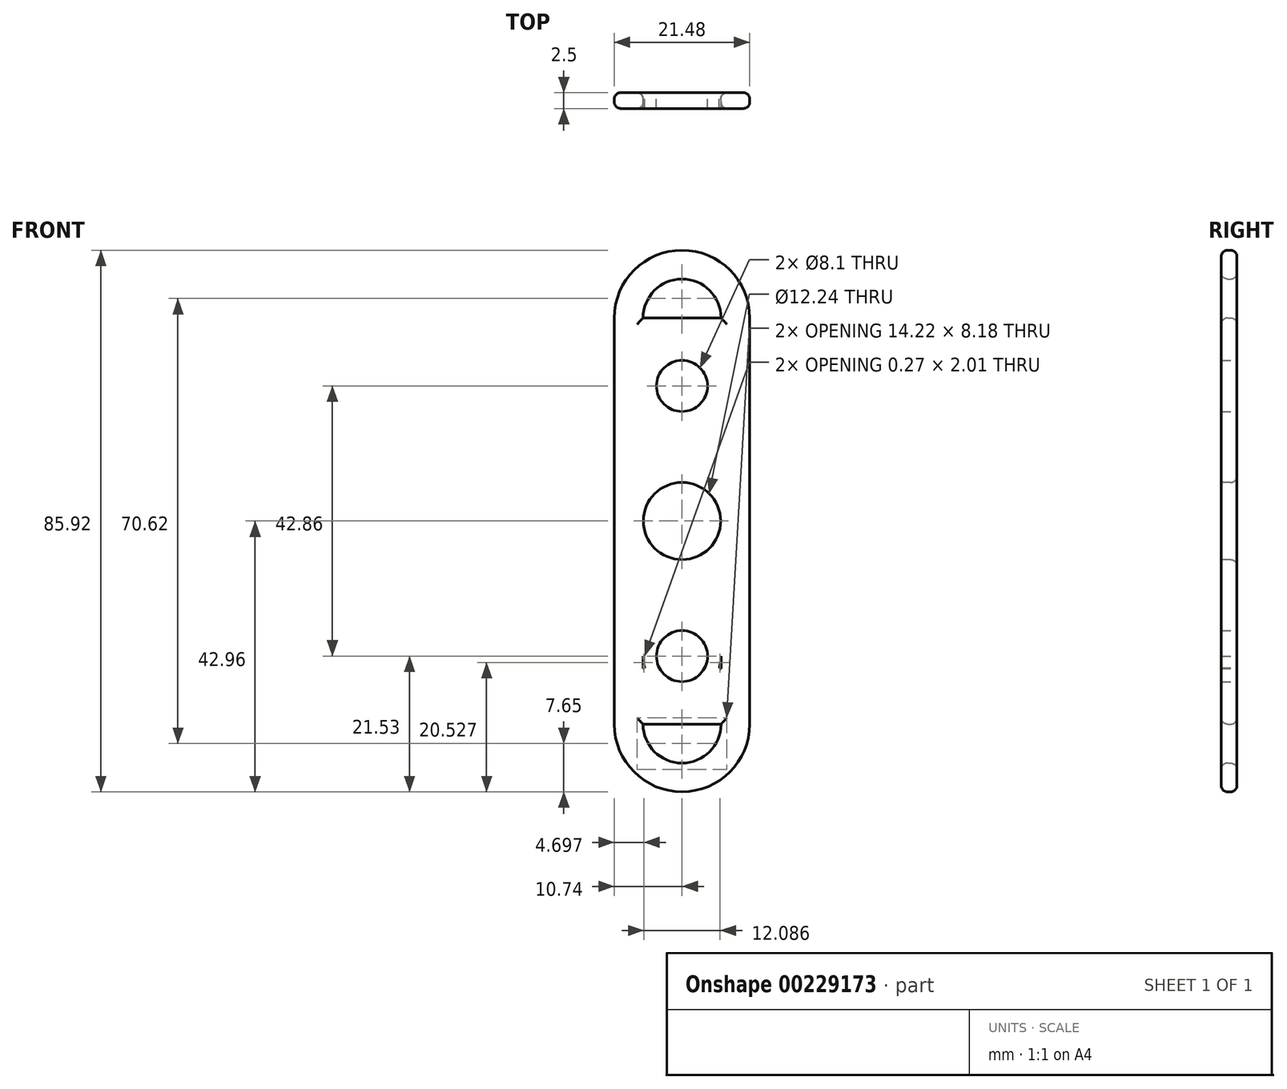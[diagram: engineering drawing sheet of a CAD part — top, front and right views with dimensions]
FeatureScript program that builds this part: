
annotation { "Feature Type Name" : "Feature", "Feature Type Description" : "" }
export const myFeature = defineFeature(function(context is Context, id is Id, definition is map)
    precondition{}
    {
        {
            var Q0;
            Q0=qCreatedBy(makeId("Front.planeOp"),FACE);
            var sketch = newSketch(context, id + "F0", { "sketchPlane" : qUnion([Q0])});
            skLineSegment(sketch, "E0.bottom", {"start": v(6.18, -11.5) * mm, "end": v(-6.18, -11.5) * mm});
            skLineSegment(sketch, "E0.top", {"start": v(6.18, 11.5) * mm, "end": v(-6.18, 11.5) * mm});
            skLineSegment(sketch, "E0.left", {"start": v(6.18, -11.5) * mm, "end": v(6.18, 11.5) * mm});
            skLineSegment(sketch, "E0.right", {"start": v(-6.18, -11.5) * mm, "end": v(-6.18, 11.5) * mm});
            skPoint(sketch, "E0.middle", {"position": v(0, 0) * mm});
            skLineSegment(sketch, "E1.bottom", {"start": v(6.18, -16.1) * mm, "end": v(-6.18, -16.1) * mm});
            skLineSegment(sketch, "E1.top", {"start": v(6.18, 16.1) * mm, "end": v(-6.18, 16.1) * mm});
            skLineSegment(sketch, "E1.left", {"start": v(6.18, -16.1) * mm, "end": v(6.18, 16.1) * mm});
            skLineSegment(sketch, "E1.right", {"start": v(-6.18, -16.1) * mm, "end": v(-6.18, 16.1) * mm});
            skLineSegment(sketch, "E2.left", {"start": v(10.74, -19) * mm, "end": v(10.74, 16.1) * mm});
            skLineSegment(sketch, "E2.right", {"start": v(-10.74, -19) * mm, "end": v(-10.74, 16.1) * mm});
            skLineSegment(sketch, "E3", {"start": v(-6.18, 16.1) * mm, "end": v(6.18, 11.5) * mm, "construction": true});
            skLineSegment(sketch, "E4", {"start": v(-6.18, 11.5) * mm, "end": v(6.18, 16.1) * mm, "construction": true});
            skArc(sketch, "E5", {"start": v(10.74, 16.1) * mm, "mid": v(0, 26.85) * mm, "end": v(-10.74, 16.1) * mm});
            skArc(sketch, "E6", {"start": v(6.18, 16.1) * mm, "mid": v(0, 22.29) * mm, "end": v(-6.18, 16.1) * mm});
            skCircle(sketch, "E7", {"center": v(0, 13.8) * mm, "radius": 1 * mm});
            skCircle(sketch, "E8", {"center": v(0, -13.8) * mm, "radius": 1 * mm});
            skLineSegment(sketch, "E9.bottom", {"start": v(-6.18, -48.33) * mm, "end": v(6.18, -48.33) * mm});
            skLineSegment(sketch, "E9.top", {"start": v(-6.18, -16.1) * mm, "end": v(6.18, -16.1) * mm});
            skLineSegment(sketch, "E9.left", {"start": v(-6.18, -48.33) * mm, "end": v(-6.18, -16.1) * mm});
            skLineSegment(sketch, "E9.right", {"start": v(6.18, -48.33) * mm, "end": v(6.18, -16.1) * mm});
            skLineSegment(sketch, "E10.bottom", {"start": v(6.18, -43.72) * mm, "end": v(-6.18, -43.72) * mm});
            skLineSegment(sketch, "E10.top", {"start": v(6.18, -20.72) * mm, "end": v(-6.18, -20.72) * mm});
            skLineSegment(sketch, "E10.left", {"start": v(6.18, -43.72) * mm, "end": v(6.18, -20.72) * mm});
            skLineSegment(sketch, "E10.right", {"start": v(-6.18, -43.72) * mm, "end": v(-6.18, -20.72) * mm});
            skLineSegment(sketch, "E11", {"start": v(-6.18, -43.72) * mm, "end": v(6.18, -48.33) * mm, "construction": true});
            skLineSegment(sketch, "E12", {"start": v(-6.18, -48.33) * mm, "end": v(6.18, -43.72) * mm, "construction": true});
            skCircle(sketch, "E13", {"center": v(0, -46.03) * mm, "radius": 1 * mm});
            skCircle(sketch, "E14", {"center": v(0, -23.42) * mm, "radius": 1 * mm});
            skPoint(sketch, "E15.center.orphan", {"position": v(0, -48.33) * mm});
            skPoint(sketch, "E16.centerSnap0", {"position": v(0, -16.1) * mm});
            skLineSegment(sketch, "E17", {"start": v(-6.18, -16.1) * mm, "end": v(-6.18, -16.1) * mm});
            skLineSegment(sketch, "E18", {"start": v(6.18, -16.1) * mm, "end": v(6.18, -16.1) * mm});
            skLineSegment(sketch, "E19", {"start": v(-10.74, -19) * mm, "end": v(-10.74, -48.33) * mm});
            skLineSegment(sketch, "E20", {"start": v(10.74, -19) * mm, "end": v(10.74, -48.33) * mm});
            skCircle(sketch, "E21", {"center": v(0, -48.33) * mm, "radius": 6.18 * mm});
            skCircle(sketch, "E22", {"center": v(0, -48.33) * mm, "radius": 10.74 * mm});
            skCircle(sketch, "E23", {"center": v(0, -37.54) * mm, "radius": 6.18 * mm});
            skCircle(sketch, "E24", {"center": v(0, 5.32) * mm, "radius": 6.18 * mm});
            skCircle(sketch, "E25", {"center": v(0, 5.32) * mm, "radius": 4.05 * mm});
            skCircle(sketch, "E26", {"center": v(0, -37.54) * mm, "radius": 4.05 * mm});
            skPoint(sketch, "E27.centerSnap0", {"position": v(6.18, -21.1) * mm});
            skSolve(sketch);
        }
        {
            var Q0;
            {var subQ4=sQuery(id+"F0.wireOp",EDGE,"E22");var subQ15=makeQuery(id+"F0.imprint","INTERSECT",VERTEX,{"derivedFrom":[sQuery(id+"F0.wireOp",EDGE,"E20"),subQ4]});Q0=makeQuery(id+"F0.imprint","IMPRINT",FACE,{"disambiguationData":[TD([[makeQuery(id+"F0.imprint","IMPRINT",EDGE,{"disambiguationData":[TD([[subQ15,-1.0]])],"derivedFrom":subQ4}),1.0]])]});}
            var Q1;
            Q1=makeQuery(id+"F0.imprint","IMPRINT",FACE,{"disambiguationData":[TD([[makeQuery(id+"F0.imprint","IMPRINT",EDGE,{"derivedFrom":sQuery(id+"F0.wireOp",EDGE,"E2.left")}),1.0]])]});
            var Q2;
            {var subQ1=sQuery(id+"F0.wireOp",EDGE,"E0.bottom");Q2=makeQuery(id+"F0.imprint","IMPRINT",FACE,{"disambiguationData":[TD([[makeQuery(id+"F0.imprint","IMPRINT",EDGE,{"derivedFrom":subQ1}),1.0]])]});}
            var Q3;
            {var subQ0=sQuery(id+"F0.wireOp",EDGE,"E0.bottom");Q3=makeQuery(id+"F0.imprint","IMPRINT",FACE,{"disambiguationData":[TD([[makeQuery(id+"F0.imprint","IMPRINT",EDGE,{"derivedFrom":subQ0}),-1.0]])]});}
            var Q4;
            {var subQ0=sQuery(id+"F0.wireOp",EDGE,"E22");var subQ1=sQuery(id+"F0.wireOp",EDGE,"E10.left");var subQ2=makeQuery(id+"F0.imprint","INTERSECT",VERTEX,{"derivedFrom":[subQ1,subQ0]});Q4=makeQuery(id+"F0.imprint","IMPRINT",FACE,{"disambiguationData":[TD([[makeQuery(id+"F0.imprint","IMPRINT",EDGE,{"disambiguationData":[TD([[subQ2,-1.0]])],"derivedFrom":subQ1}),1.0]])]});}
            var Q5;
            {var subQ0=sQuery(id+"F0.wireOp",EDGE,"E10.top");Q5=makeQuery(id+"F0.imprint","IMPRINT",FACE,{"disambiguationData":[TD([[makeQuery(id+"F0.imprint","IMPRINT",EDGE,{"derivedFrom":subQ0}),1.0]])]});}
            var Q6;
            {var subQ5=sQuery(id+"F0.wireOp",EDGE,"E21");var subQ6=sQuery(id+"F0.wireOp",EDGE,"E10.bottom");var subQ7=makeQuery(id+"F0.imprint","INTERSECT",VERTEX,{"disambiguationData":[OD(0.0)],"derivedFrom":[subQ6,subQ5]});Q6=makeQuery(id+"F0.imprint","IMPRINT",FACE,{"disambiguationData":[TD([[makeQuery(id+"F0.imprint","IMPRINT",EDGE,{"disambiguationData":[TD([[subQ7,-1.0]])],"derivedFrom":subQ5}),-1.0]])]});}
            var Q7;
            {var subQ0=sQuery(id+"F0.wireOp",EDGE,"E21");var subQ1=sQuery(id+"F0.wireOp",EDGE,"E10.bottom");var subQ2=makeQuery(id+"F0.imprint","INTERSECT",VERTEX,{"disambiguationData":[OD(0.0)],"derivedFrom":[subQ1,subQ0]});Q7=makeQuery(id+"F0.imprint","IMPRINT",FACE,{"disambiguationData":[TD([[makeQuery(id+"F0.imprint","IMPRINT",EDGE,{"disambiguationData":[TD([[subQ2,-1.0]])],"derivedFrom":subQ1}),-1.0]])]});}
            var Q8;
            {var subQ5=sQuery(id+"F0.wireOp",EDGE,"E9.bottom");Q8=makeQuery(id+"F0.imprint","IMPRINT",FACE,{"disambiguationData":[TD([[makeQuery(id+"F0.imprint","IMPRINT",EDGE,{"derivedFrom":subQ5}),1.0]])]});}
            var Q9;
            {var subQ0=sQuery(id+"F0.wireOp",EDGE,"E21");var subQ3=sQuery(id+"F0.wireOp",EDGE,"E10.bottom");var subQ5=makeQuery(id+"F0.imprint","INTERSECT",VERTEX,{"disambiguationData":[OD(1.0)],"derivedFrom":[subQ3,subQ0]});Q9=makeQuery(id+"F0.imprint","IMPRINT",FACE,{"disambiguationData":[TD([[makeQuery(id+"F0.imprint","IMPRINT",EDGE,{"disambiguationData":[TD([[subQ5,-1.0]])],"derivedFrom":subQ3}),1.0]])]});}
            var Q10;
            {var subQ0=sQuery(id+"F0.wireOp",EDGE,"E21");var subQ3=sQuery(id+"F0.wireOp",EDGE,"E10.bottom");var subQ5=makeQuery(id+"F0.imprint","INTERSECT",VERTEX,{"disambiguationData":[OD(0.0)],"derivedFrom":[subQ3,subQ0]});Q10=makeQuery(id+"F0.imprint","IMPRINT",FACE,{"disambiguationData":[TD([[makeQuery(id+"F0.imprint","IMPRINT",EDGE,{"disambiguationData":[TD([[subQ5,1.0]])],"derivedFrom":subQ3}),1.0]])]});}
            var Q11;
            {var subQ3=sQuery(id+"F0.wireOp",EDGE,"E10.top");Q11=makeQuery(id+"F0.imprint","IMPRINT",FACE,{"disambiguationData":[TD([[makeQuery(id+"F0.imprint","IMPRINT",EDGE,{"derivedFrom":subQ3}),-1.0]])]});}
            var Q12;
            Q12=makeQuery(id+"F0.imprint","IMPRINT",FACE,{"disambiguationData":[TD([[makeQuery(id+"F0.imprint","IMPRINT",EDGE,{"derivedFrom":sQuery(id+"F0.wireOp",EDGE,"E13")}),1.0]])]});
            var Q13;
            {var subQ5=sQuery(id+"F0.wireOp",EDGE,"E21");var subQ6=sQuery(id+"F0.wireOp",EDGE,"E10.bottom");var subQ7=makeQuery(id+"F0.imprint","INTERSECT",VERTEX,{"disambiguationData":[OD(1.0)],"derivedFrom":[subQ6,subQ5]});Q13=makeQuery(id+"F0.imprint","IMPRINT",FACE,{"disambiguationData":[TD([[makeQuery(id+"F0.imprint","IMPRINT",EDGE,{"disambiguationData":[TD([[subQ7,1.0]])],"derivedFrom":subQ5}),-1.0]])]});}
            var Q14;
            {var subQ0=sQuery(id+"F0.wireOp",EDGE,"E23");var subQ1=sQuery(id+"F0.wireOp",EDGE,"E10.bottom");var subQ2=makeQuery(id+"F0.imprint","INTERSECT",VERTEX,{"derivedFrom":[subQ1,subQ0]});Q14=makeQuery(id+"F0.imprint","IMPRINT",FACE,{"disambiguationData":[TD([[makeQuery(id+"F0.imprint","IMPRINT",EDGE,{"disambiguationData":[TD([[subQ2,-1.0]])],"derivedFrom":subQ1}),-1.0]])]});}
            var Q15;
            {var subQ0=sQuery(id+"F0.wireOp",EDGE,"E23");var subQ3=sQuery(id+"F0.wireOp",EDGE,"E22");var subQ8=makeQuery(id+"F0.imprint","INTERSECT",VERTEX,{"disambiguationData":[OD(0.0)],"derivedFrom":[subQ3,subQ0]});Q15=makeQuery(id+"F0.imprint","IMPRINT",FACE,{"disambiguationData":[TD([[makeQuery(id+"F0.imprint","IMPRINT",EDGE,{"disambiguationData":[TD([[subQ8,-1.0]])],"derivedFrom":subQ3}),-1.0]])]});}
            var Q16;
            {var subQ0=sQuery(id+"F0.wireOp",EDGE,"E23");var subQ1=sQuery(id+"F0.wireOp",EDGE,"E21");var subQ9=makeQuery(id+"F0.imprint","INTERSECT",VERTEX,{"disambiguationData":[OD(0.0)],"derivedFrom":[subQ1,subQ0]});Q16=makeQuery(id+"F0.imprint","IMPRINT",FACE,{"disambiguationData":[TD([[makeQuery(id+"F0.imprint","IMPRINT",EDGE,{"disambiguationData":[TD([[subQ9,-1.0]])],"derivedFrom":subQ1}),-1.0]])]});}
            var Q17;
            {var subQ0=sQuery(id+"F0.wireOp",EDGE,"E23");var subQ1=sQuery(id+"F0.wireOp",EDGE,"E21");var subQ2=makeQuery(id+"F0.imprint","INTERSECT",VERTEX,{"disambiguationData":[OD(0.0)],"derivedFrom":[subQ1,subQ0]});Q17=makeQuery(id+"F0.imprint","IMPRINT",FACE,{"disambiguationData":[TD([[makeQuery(id+"F0.imprint","IMPRINT",EDGE,{"disambiguationData":[TD([[subQ2,-1.0]])],"derivedFrom":subQ1}),1.0]])]});}
            var Q18;
            {var subQ0=sQuery(id+"F0.wireOp",EDGE,"E22");var subQ1=sQuery(id+"F0.wireOp",EDGE,"E10.right");var subQ2=makeQuery(id+"F0.imprint","INTERSECT",VERTEX,{"derivedFrom":[subQ1,subQ0]});Q18=makeQuery(id+"F0.imprint","IMPRINT",FACE,{"disambiguationData":[TD([[makeQuery(id+"F0.imprint","IMPRINT",EDGE,{"disambiguationData":[TD([[subQ2,-1.0]])],"derivedFrom":subQ1}),-1.0]])]});}
            var Q19;
            Q19=makeQuery(id+"F0.imprint","IMPRINT",FACE,{"disambiguationData":[TD([[makeQuery(id+"F0.imprint","IMPRINT",EDGE,{"derivedFrom":sQuery(id+"F0.wireOp",EDGE,"E25")}),-1.0]])]});
            var Q20;
            {var subQ0=sQuery(id+"F0.wireOp",EDGE,"E1.right");var subQ1=sQuery(id+"F0.wireOp",EDGE,"E0.top");var subQ2=makeQuery(id+"F0.imprint","INTERSECT",VERTEX,{"derivedFrom":[subQ1,subQ0]});Q20=makeQuery(id+"F0.imprint","IMPRINT",FACE,{"disambiguationData":[TD([[makeQuery(id+"F0.imprint","IMPRINT",EDGE,{"disambiguationData":[TD([[subQ2,1.0]])],"derivedFrom":subQ1}),1.0]])]});}
            var Q21;
            {var subQ4=sQuery(id+"F0.wireOp",EDGE,"E1.top");Q21=makeQuery(id+"F0.imprint","IMPRINT",FACE,{"disambiguationData":[TD([[makeQuery(id+"F0.imprint","IMPRINT",EDGE,{"derivedFrom":subQ4}),1.0]])]});}
            var Q22;
            {var subQ0=sQuery(id+"F0.wireOp",EDGE,"E1.left");var subQ1=sQuery(id+"F0.wireOp",EDGE,"E0.top");var subQ2=makeQuery(id+"F0.imprint","INTERSECT",VERTEX,{"derivedFrom":[subQ1,subQ0]});Q22=makeQuery(id+"F0.imprint","IMPRINT",FACE,{"disambiguationData":[TD([[makeQuery(id+"F0.imprint","IMPRINT",EDGE,{"disambiguationData":[TD([[subQ2,-1.0]])],"derivedFrom":subQ1}),1.0]])]});}
            var Q23;
            Q23=makeQuery(id+"F0.imprint","IMPRINT",FACE,{"disambiguationData":[TD([[makeQuery(id+"F0.imprint","IMPRINT",EDGE,{"derivedFrom":sQuery(id+"F0.wireOp",EDGE,"E7")}),1.0]])]});
            var Q24;
            Q24=makeQuery(id+"F0.imprint","IMPRINT",FACE,{"disambiguationData":[TD([[makeQuery(id+"F0.imprint","IMPRINT",EDGE,{"derivedFrom":sQuery(id+"F0.wireOp",EDGE,"E8")}),1.0]])]});
            var Q25;
            Q25=makeQuery(id+"F0.imprint","IMPRINT",FACE,{"disambiguationData":[TD([[makeQuery(id+"F0.imprint","IMPRINT",EDGE,{"derivedFrom":sQuery(id+"F0.wireOp",EDGE,"E14")}),-1.0]])]});
            var Q26;
            {var subQ0=sQuery(id+"F0.wireOp",EDGE,"E27");var subQ1=sQuery(id+"F0.wireOp",EDGE,"E1.bottom");var subQ2=makeQuery(id+"F0.imprint","INTERSECT",VERTEX,{"disambiguationData":[OD(0.0)],"derivedFrom":[subQ1,subQ0]});Q26=makeQuery(id+"F0.imprint","IMPRINT",FACE,{"disambiguationData":[TD([[makeQuery(id+"F0.imprint","IMPRINT",EDGE,{"disambiguationData":[TD([[subQ2,-1.0]])],"derivedFrom":subQ1}),-1.0]])]});}
            var Q27;
            {var subQ0=sQuery(id+"F0.wireOp",EDGE,"E27");var subQ1=sQuery(id+"F0.wireOp",EDGE,"E9.top");var subQ2=makeQuery(id+"F0.imprint","INTERSECT",VERTEX,{"disambiguationData":[OD(0.0)],"derivedFrom":[subQ1,subQ0]});Q27=makeQuery(id+"F0.imprint","IMPRINT",FACE,{"disambiguationData":[TD([[makeQuery(id+"F0.imprint","IMPRINT",EDGE,{"disambiguationData":[TD([[subQ2,-1.0]])],"derivedFrom":subQ1}),-1.0]])]});}
            var Q28;
            Q28=makeQuery(id+"F0.imprint","IMPRINT",FACE,{"disambiguationData":[TD([[makeQuery(id+"F0.imprint","IMPRINT",EDGE,{"derivedFrom":sQuery(id+"F0.wireOp",EDGE,"E14")}),1.0]])]});
            extrude(context, id + "F1", {"entities" : qUnion([Q0, Q1, Q2, Q3, Q4, Q5, Q6, Q7, Q8, Q9, Q10, Q11, Q12, Q13, Q14, Q15, Q16, Q17, Q18, Q19, Q20, Q21, Q22, Q23, Q24, Q25, Q26, Q27, Q28]), "depth" : 2.5 * mm});
        }
        {
            var Q0;
            Q0=makeQuery(id+"F1.opExtrude","CAP_FACE",FACE,{"disambiguationData":[OSD([sQuery(id+"F0.wireOp",EDGE,"E1.top"),sQuery(id+"F0.wireOp",EDGE,"E2.left"),sQuery(id+"F0.wireOp",EDGE,"E2.right"),sQuery(id+"F0.wireOp",EDGE,"E5"),sQuery(id+"F0.wireOp",EDGE,"E6"),sQuery(id+"F0.wireOp",EDGE,"E9.bottom"),sQuery(id+"F0.wireOp",EDGE,"E19"),sQuery(id+"F0.wireOp",EDGE,"E20"),sQuery(id+"F0.wireOp",EDGE,"E21"),sQuery(id+"F0.wireOp",EDGE,"E22"),sQuery(id+"F0.wireOp",EDGE,"E25"),sQuery(id+"F0.wireOp",EDGE,"E26")])],"isStart":false});
            var sketch = newSketch(context, id + "F2", { "sketchPlane" : qUnion([Q0])});
            skCircle(sketch, "E28", {"center": v(0, -16.1) * mm, "radius": 6.12 * mm});
            skSolve(sketch);
        }
        {
            var Q0;
            Q0=makeQuery(id+"F2.imprint","IMPRINT",FACE,{"disambiguationData":[TD([[makeQuery(id+"F2.imprint","IMPRINT",EDGE,{"derivedFrom":sQuery(id+"F2.wireOp",EDGE,"E28")}),1.0]])]});
            extrude(context, id + "F3", {"entities" : qUnion([Q0]), "operationType" : NewBodyOperationType.REMOVE, "oppositeDirection" : true, "depth" : 25 * mm});
        }
        {
            var Q0;
            Q0=makeQuery(id+"F1.opExtrude","CAP_EDGE",EDGE,{"disambiguationData":[OSD([sQuery(id+"F0.wireOp",EDGE,"E2.right"),sQuery(id+"F0.wireOp",EDGE,"E19")])],"isStart":false});
            var Q1;
            Q1=makeQuery(id+"F1.opExtrude","CAP_EDGE",EDGE,{"disambiguationData":[OSD([sQuery(id+"F0.wireOp",EDGE,"E21")])],"isStart":false});
            var Q2;
            Q2=makeQuery(id+"F1.opExtrude","CAP_EDGE",EDGE,{"disambiguationData":[OSD([sQuery(id+"F0.wireOp",EDGE,"E9.bottom")])],"isStart":false});
            var Q3;
            Q3=makeQuery(id+"F1.opExtrude","CAP_EDGE",EDGE,{"disambiguationData":[OSD([sQuery(id+"F0.wireOp",EDGE,"E2.left"),sQuery(id+"F0.wireOp",EDGE,"E20")])],"isStart":true});
            var Q4;
            Q4=makeQuery(id+"F3.boolean.opBoolean","INTERSECT",EDGE,{"derivedFrom":[makeQuery(id+"F1.opExtrude","CAP_FACE",FACE,{"disambiguationData":[OSD([sQuery(id+"F0.wireOp",EDGE,"E1.top"),sQuery(id+"F0.wireOp",EDGE,"E2.left"),sQuery(id+"F0.wireOp",EDGE,"E2.right"),sQuery(id+"F0.wireOp",EDGE,"E5"),sQuery(id+"F0.wireOp",EDGE,"E6"),sQuery(id+"F0.wireOp",EDGE,"E9.bottom"),sQuery(id+"F0.wireOp",EDGE,"E19"),sQuery(id+"F0.wireOp",EDGE,"E20"),sQuery(id+"F0.wireOp",EDGE,"E21"),sQuery(id+"F0.wireOp",EDGE,"E22"),sQuery(id+"F0.wireOp",EDGE,"E25"),sQuery(id+"F0.wireOp",EDGE,"E26")])],"isStart":true}),makeQuery(id+"F3.opExtrude","SWEPT_FACE",FACE,{"disambiguationData":[OSD([sQuery(id+"F2.wireOp",EDGE,"E28")])]})]});
            var Q5;
            Q5=makeQuery(id+"F3.boolean.opBoolean","COPY",EDGE,{"derivedFrom":makeQuery(id+"F3.opExtrude","CAP_EDGE",EDGE,{"disambiguationData":[OSD([sQuery(id+"F2.wireOp",EDGE,"E28")])],"isStart":true})});
            var Q6;
            Q6=makeQuery(id+"F1.opExtrude","CAP_EDGE",EDGE,{"disambiguationData":[OSD([sQuery(id+"F0.wireOp",EDGE,"E1.top")])],"isStart":false});
            var Q7;
            Q7=makeQuery(id+"F1.opExtrude","CAP_EDGE",EDGE,{"disambiguationData":[OSD([sQuery(id+"F0.wireOp",EDGE,"E6")])],"isStart":false});
            var Q8;
            Q8=makeQuery(id+"F1.opExtrude","CAP_EDGE",EDGE,{"disambiguationData":[OSD([sQuery(id+"F0.wireOp",EDGE,"E1.top")])],"isStart":true});
            var Q9;
            Q9=makeQuery(id+"F1.opExtrude","CAP_EDGE",EDGE,{"disambiguationData":[OSD([sQuery(id+"F0.wireOp",EDGE,"E6")])],"isStart":true});
            var Q10;
            Q10=makeQuery(id+"F1.opExtrude","CAP_EDGE",EDGE,{"disambiguationData":[OSD([sQuery(id+"F0.wireOp",EDGE,"E9.bottom")])],"isStart":true});
            var Q11;
            Q11=makeQuery(id+"F1.opExtrude","CAP_EDGE",EDGE,{"disambiguationData":[OSD([sQuery(id+"F0.wireOp",EDGE,"E21")])],"isStart":true});
            fillet(context, id + "F4", {"entities" : qUnion([Q0, Q1, Q2, Q3, Q4, Q5, Q6, Q7, Q8, Q9, Q10, Q11]), "radius" : 1 * mm, "tangentPropagation" : true, "allowEdgeOverflow" : false});
        }
    });
